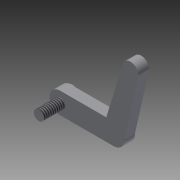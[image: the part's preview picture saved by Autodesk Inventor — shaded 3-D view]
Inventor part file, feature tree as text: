
AUTODESK INVENTOR PART (.ipt)
format: ipt  version: 2015 SP2 (Build 190223200, 223)  size: 99,840 bytes
history: native  units: mm
features: extrude x3, sketch x3, thread x1
ambient origin geometry x8: Origin, YZ Plane, XZ Plane, XY Plane, X Axis, Y Axis, Z Axis, Center Point
bodies: Solid1 (feature_tree)
feature tree (7):
  extrude  "Extrusion1"  Depth=4.0mm
  extrude  "Extrusion2"  Depth=2.0mm TaperAngle=0.0deg
  thread  "Thread1"  [1 undecoded]
  extrude  "Extrusion3"  Depth=0.3mm TaperAngle=0.0deg
  sketch  "Sketch1"  dims[d0=4.0mm d1=1.9mm]
  sketch  "Sketch2"  dims[d2=3.0mm d3=2.0mm d4=0.0mm d5=6.0mm d6=0.5mm d7=0.0mm d8=0.0mm]
  sketch  "Sketch3"  dims[d9=10.0mm d10=0.0mm d11=0.3mm d12=0.0mm]
note: 1 required parameter value undecoded (feature->parameter linkage not recoverable at this tier; creation-order binding heuristic only, values carry confidence <= 0.55)
